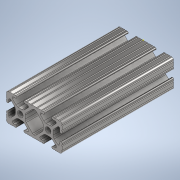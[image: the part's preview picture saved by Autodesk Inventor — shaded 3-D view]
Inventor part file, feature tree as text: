
AUTODESK INVENTOR PART (.ipt)
format: ipt  version: 2020 (Build 240168000, 168)  size: 345,088 bytes
history: native  units: in
note: dims shown in document units (in); Inventor stores cm internally (conversion verified against a paired STEP export)
features: sketch x2, extrude x1
ambient origin geometry x8: Origin, YZ Plane, XZ Plane, XY Plane, X Axis, Y Axis, Z Axis, Center Point
bodies: Solid1 (feature_tree)
feature tree (3):
  extrude  "Extrusion1"  [1 undecoded]
  sketch  "Sketch2"
  sketch  "Sketch1"  dims[d0=4.0in d1=0.0in]
note: 1 required parameter value undecoded (feature->parameter linkage not recoverable at this tier; creation-order binding heuristic only, values carry confidence <= 0.55)
